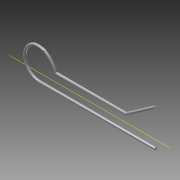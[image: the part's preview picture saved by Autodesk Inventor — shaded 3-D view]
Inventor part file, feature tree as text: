
AUTODESK INVENTOR PART (.ipt)
format: ipt  version: 2013 (Build 170138000, 138)  size: 110,592 bytes
history: native  units: in
note: dims shown in document units (in); Inventor stores cm internally (conversion verified against a paired STEP export)
features: sketch x4, plane x2, sweep x1, other x1
ambient origin geometry x8: Origin, YZ Plane, XZ Plane, XY Plane, X Axis, Y Axis, Z Axis, Center Point
bodies: Solid1 (feature_tree)
feature tree (8):
  sweep  "Sweep1"
  sketch  "Sketch3"  dims[d4=0.0025in]
  plane  "Work Plane2"
  sketch  "Sketch4"  dims[d5=0.0in d6=0.0in d7=-0.1in]
  other  "Work Axis1"
  sketch  "Sketch1"  dims[d0=0.6in d2=0.45in]
  sketch  "Sketch2"  dims[d3=0.2405in]
  plane  "Work Plane1"
